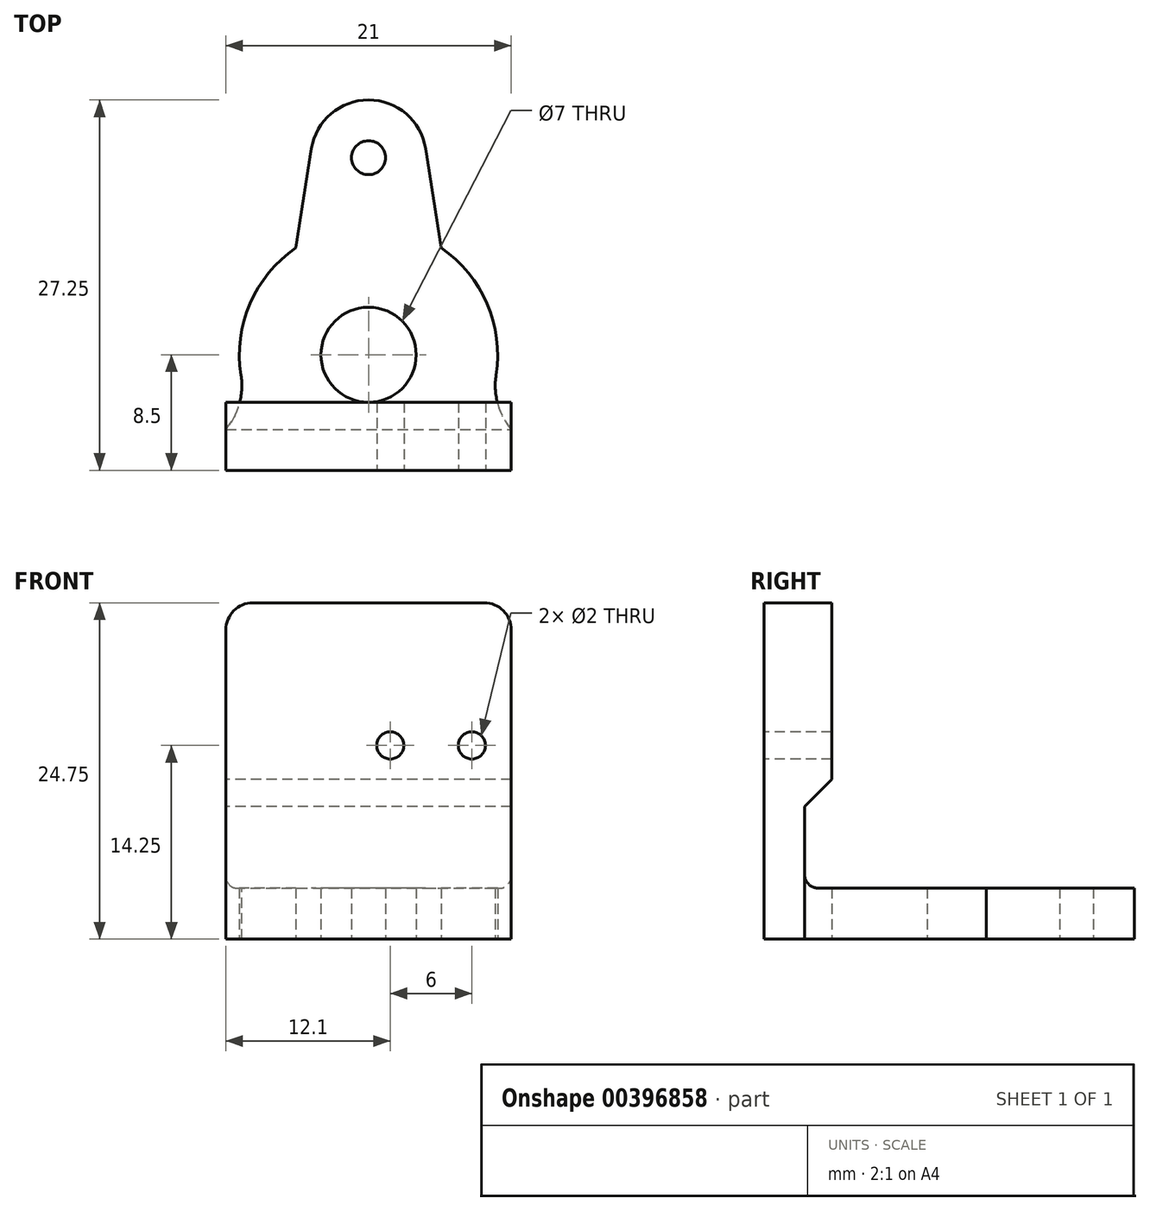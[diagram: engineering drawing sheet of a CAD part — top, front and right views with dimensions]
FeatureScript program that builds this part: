
annotation { "Feature Type Name" : "Feature", "Feature Type Description" : "" }
export const myFeature = defineFeature(function(context is Context, id is Id, definition is map)
    precondition{}
    {
        {
            var Q0;
            Q0=qCreatedBy(makeId("Top.planeOp"),FACE);
            var sketch = newSketch(context, id + "F0", { "sketchPlane" : qUnion([Q0])});
            skCircle(sketch, "E0", {"center": v(0, 0) * mm, "radius": 3.5 * mm});
            skCircle(sketch, "E1", {"center": v(0, 14.5) * mm, "radius": 1.25 * mm});
            skCircle(sketch, "E2", {"center": v(0, 0) * mm, "radius": 6.5 * mm});
            skLineSegment(sketch, "E3.bottom", {"start": v(6.5, 0) * mm, "end": v(-6.5, 0) * mm});
            skLineSegment(sketch, "E3.top", {"start": v(6.5, -8.5) * mm, "end": v(-6.5, -8.5) * mm});
            skLineSegment(sketch, "E3.left", {"start": v(6.5, -8.5) * mm, "end": v(6.5, 0) * mm});
            skLineSegment(sketch, "E3.right", {"start": v(-6.5, -8.5) * mm, "end": v(-6.5, 0) * mm});
            skCircle(sketch, "E4", {"center": v(0, 14.5) * mm, "radius": 4.25 * mm});
            skLineSegment(sketch, "E5", {"start": v(-6.42, 1) * mm, "end": v(-4.2, 15.16) * mm});
            skLineSegment(sketch, "E6", {"start": v(4.2, 15.16) * mm, "end": v(6.42, 1) * mm});
            skCircle(sketch, "E7", {"center": v(0, 0) * mm, "radius": 9.5 * mm});
            skSolve(sketch);
        }
        {
            var Q0;
            {var subQ0=sQuery(id+"F0.wireOp",EDGE,"E3.left");var subQ1=sQuery(id+"F0.wireOp",EDGE,"E3.top");var subQ2=makeQuery(id+"F0.imprint","INTERSECT",VERTEX,{"derivedFrom":[subQ1,subQ0]});Q0=makeQuery(id+"F0.imprint","IMPRINT",FACE,{"disambiguationData":[TD([[makeQuery(id+"F0.imprint","IMPRINT",EDGE,{"disambiguationData":[TD([[subQ2,-1.0]])],"derivedFrom":subQ1}),-1.0]])]});}
            var Q1;
            {var subQ0=sQuery(id+"F0.wireOp",EDGE,"E3.right");var subQ1=sQuery(id+"F0.wireOp",EDGE,"E3.top");var subQ2=makeQuery(id+"F0.imprint","INTERSECT",VERTEX,{"derivedFrom":[subQ1,subQ0]});Q1=makeQuery(id+"F0.imprint","IMPRINT",FACE,{"disambiguationData":[TD([[makeQuery(id+"F0.imprint","IMPRINT",EDGE,{"disambiguationData":[TD([[subQ2,1.0]])],"derivedFrom":subQ1}),-1.0]])]});}
            var Q2;
            Q2=makeQuery(id+"F0.imprint","IMPRINT",FACE,{"disambiguationData":[TD([[makeQuery(id+"F0.imprint","IMPRINT",EDGE,{"derivedFrom":sQuery(id+"F0.wireOp",EDGE,"E1")}),-1.0]])]});
            var Q3;
            {var subQ0=sQuery(id+"F0.wireOp",EDGE,"E5");var subQ1=sQuery(id+"F0.wireOp",EDGE,"E4");var subQ2=makeQuery(id+"F0.imprint","INTERSECT",VERTEX,{"derivedFrom":[subQ1,subQ0]});Q3=makeQuery(id+"F0.imprint","IMPRINT",FACE,{"disambiguationData":[TD([[makeQuery(id+"F0.imprint","IMPRINT",EDGE,{"disambiguationData":[TD([[subQ2,-1.0]])],"derivedFrom":subQ1}),-1.0]])]});}
            var Q4;
            {var subQ1=sQuery(id+"F0.wireOp",EDGE,"E2");var subQ3=sQuery(id+"F0.wireOp",EDGE,"E6");var subQ4=makeQuery(id+"F0.imprint","INTERSECT",VERTEX,{"derivedFrom":[subQ1,subQ3]});Q4=makeQuery(id+"F0.imprint","IMPRINT",FACE,{"disambiguationData":[TD([[makeQuery(id+"F0.imprint","IMPRINT",EDGE,{"disambiguationData":[TD([[subQ4,1.0]])],"derivedFrom":subQ3}),1.0]])]});}
            var Q5;
            {var subQ1=sQuery(id+"F0.wireOp",EDGE,"E2");var subQ3=sQuery(id+"F0.wireOp",EDGE,"E5");var subQ4=makeQuery(id+"F0.imprint","INTERSECT",VERTEX,{"derivedFrom":[subQ1,subQ3]});Q5=makeQuery(id+"F0.imprint","IMPRINT",FACE,{"disambiguationData":[TD([[makeQuery(id+"F0.imprint","IMPRINT",EDGE,{"disambiguationData":[TD([[subQ4,-1.0]])],"derivedFrom":subQ3}),1.0]])]});}
            var Q6;
            {var subQ0=sQuery(id+"F0.wireOp",EDGE,"E5");var subQ1=sQuery(id+"F0.wireOp",EDGE,"E2");var subQ2=makeQuery(id+"F0.imprint","INTERSECT",VERTEX,{"derivedFrom":[subQ1,subQ0]});Q6=makeQuery(id+"F0.imprint","IMPRINT",FACE,{"disambiguationData":[TD([[makeQuery(id+"F0.imprint","IMPRINT",EDGE,{"disambiguationData":[TD([[subQ2,1.0]])],"derivedFrom":subQ1}),-1.0]])]});}
            var Q7;
            {var subQ4=sQuery(id+"F0.wireOp",EDGE,"E7");var subQ6=sQuery(id+"F0.wireOp",EDGE,"E3.top");var subQ11=makeQuery(id+"F0.imprint","INTERSECT",VERTEX,{"disambiguationData":[OD(0.0)],"derivedFrom":[subQ6,subQ4]});Q7=makeQuery(id+"F0.imprint","IMPRINT",FACE,{"disambiguationData":[TD([[makeQuery(id+"F0.imprint","IMPRINT",EDGE,{"disambiguationData":[TD([[subQ11,-1.0]])],"derivedFrom":subQ6}),-1.0]])]});}
            var Q8;
            {var subQ0=sQuery(id+"F0.wireOp",EDGE,"E3.bottom");var subQ1=sQuery(id+"F0.wireOp",EDGE,"E0");var subQ2=makeQuery(id+"F0.imprint","INTERSECT",VERTEX,{"disambiguationData":[OD(0.0)],"derivedFrom":[subQ1,subQ0]});Q8=makeQuery(id+"F0.imprint","IMPRINT",FACE,{"disambiguationData":[TD([[makeQuery(id+"F0.imprint","IMPRINT",EDGE,{"disambiguationData":[TD([[subQ2,1.0]])],"derivedFrom":subQ1}),-1.0]])]});}
            var Q9;
            {var subQ3=sQuery(id+"F0.wireOp",EDGE,"E3.bottom");var subQ6=sQuery(id+"F0.wireOp",EDGE,"E0");var subQ7=makeQuery(id+"F0.imprint","INTERSECT",VERTEX,{"disambiguationData":[OD(0.0)],"derivedFrom":[subQ6,subQ3]});Q9=makeQuery(id+"F0.imprint","IMPRINT",FACE,{"disambiguationData":[TD([[makeQuery(id+"F0.imprint","IMPRINT",EDGE,{"disambiguationData":[TD([[subQ7,-1.0]])],"derivedFrom":subQ6}),-1.0]])]});}
            extrude(context, id + "F1", {"entities" : qUnion([Q0, Q1, Q2, Q3, Q4, Q5, Q6, Q7, Q8, Q9]), "depth" : 3.75 * mm});
        }
        {
            var Q0;
            Q0=makeQuery(id+"F1.opExtrude","SWEPT_FACE",FACE,{"disambiguationData":[OSD([sQuery(id+"F0.wireOp",EDGE,"E3.top")])]});
            cPlane(context, id + "F2", {"entities" : qUnion([Q0]), "cplaneType" : CPlaneType.OFFSET, "offset" : 0 * mm, "width" : 150 * mm, "height" : 150 * mm});
        }
        {
            var Q0;
            Q0=qCreatedBy(id+"F2.planeOp",FACE);
            var sketch = newSketch(context, id + "F3", { "sketchPlane" : qUnion([Q0])});
            skLineSegment(sketch, "E8.bottom", {"start": v(-10.5, 24.75) * mm, "end": v(10.5, 24.75) * mm});
            skLineSegment(sketch, "E8.top", {"start": v(-10.5, 3.75) * mm, "end": v(10.5, 3.75) * mm});
            skLineSegment(sketch, "E8.left", {"start": v(-10.5, 24.75) * mm, "end": v(-10.5, 3.75) * mm});
            skLineSegment(sketch, "E8.right", {"start": v(10.5, 24.75) * mm, "end": v(10.5, 3.75) * mm});
            skLineSegment(sketch, "E9.bottom", {"start": v(-6.5, 3.75) * mm, "end": v(6.5, 3.75) * mm});
            skLineSegment(sketch, "E9.top", {"start": v(-6.5, 0) * mm, "end": v(6.5, 0) * mm});
            skLineSegment(sketch, "E9.left", {"start": v(-6.5, 3.75) * mm, "end": v(-6.5, 0) * mm});
            skLineSegment(sketch, "E9.right", {"start": v(6.5, 3.75) * mm, "end": v(6.5, 0) * mm});
            skLineSegment(sketch, "E10", {"start": v(0, 24.75) * mm, "end": v(0, 0) * mm});
            skLineSegment(sketch, "E11.top", {"start": v(-10.5, 0) * mm, "end": v(10.5, 0) * mm});
            skLineSegment(sketch, "E11.left", {"start": v(-10.5, 3.75) * mm, "end": v(-10.5, 0) * mm});
            skLineSegment(sketch, "E11.right", {"start": v(10.5, 3.75) * mm, "end": v(10.5, 0) * mm});
            skSolve(sketch);
        }
        {
            var Q0;
            {var subQ0=sQuery(id+"F3.wireOp",EDGE,"E9.left");var subQ4=sQuery(id+"F3.wireOp",EDGE,"E8.left");var subQ12=sQuery(id+"F3.wireOp",EDGE,"E8.right");var subQ14=sQuery(id+"F3.wireOp",EDGE,"E9.right");var subQ23=makeQuery(id+"F3.imprint","IMPRINT",EDGE,{"derivedFrom":subQ14});var subQ24=makeQuery(id+"F3.imprint","IMPRINT",EDGE,{"derivedFrom":subQ0});Q0=qUnion([makeQuery(id+"F3.imprint","IMPRINT",FACE,{"disambiguationData":[TD([[subQ23,1.0]])]}),makeQuery(id+"F3.imprint","IMPRINT",FACE,{"disambiguationData":[TD([[subQ24,1.0]])]}),makeQuery(id+"F3.imprint","IMPRINT",FACE,{"disambiguationData":[TD([[subQ24,-1.0]])]}),makeQuery(id+"F3.imprint","IMPRINT",FACE,{"disambiguationData":[TD([[subQ23,-1.0]])]}),makeQuery(id+"F3.imprint","IMPRINT",FACE,{"disambiguationData":[TD([[makeQuery(id+"F3.imprint","IMPRINT",EDGE,{"derivedFrom":subQ12}),-1.0]])]}),makeQuery(id+"F3.imprint","IMPRINT",FACE,{"disambiguationData":[TD([[makeQuery(id+"F3.imprint","IMPRINT",EDGE,{"derivedFrom":subQ4}),1.0]])]})]);}
            extrude(context, id + "F4", {"entities" : qUnion([Q0]), "operationType" : NewBodyOperationType.ADD, "oppositeDirection" : true, "depth" : 3 * mm});
        }
        {
            var Q0;
            Q0=makeQuery(id+"F4.opExtrude","CAP_FACE",FACE,{"disambiguationData":[OSD([sQuery(id+"F3.wireOp",EDGE,"E8.bottom"),sQuery(id+"F3.wireOp",EDGE,"E8.left"),sQuery(id+"F3.wireOp",EDGE,"E8.right"),sQuery(id+"F3.wireOp",EDGE,"E9.top"),sQuery(id+"F3.wireOp",EDGE,"E11.top"),sQuery(id+"F3.wireOp",EDGE,"E11.left"),sQuery(id+"F3.wireOp",EDGE,"E11.right")])],"isStart":false});
            var sketch = newSketch(context, id + "F5", { "sketchPlane" : qUnion([Q0])});
            skLineSegment(sketch, "E12.bottom", {"start": v(-10.5, 24.75) * mm, "end": v(10.5, 24.75) * mm});
            skLineSegment(sketch, "E12.top", {"start": v(-10.5, 9.75) * mm, "end": v(10.5, 9.75) * mm});
            skLineSegment(sketch, "E12.left", {"start": v(-10.5, 24.75) * mm, "end": v(-10.5, 9.75) * mm});
            skLineSegment(sketch, "E12.right", {"start": v(10.5, 24.75) * mm, "end": v(10.5, 9.75) * mm});
            skSolve(sketch);
        }
        {
            var Q0;
            Q0=makeQuery(id+"F5.imprint","IMPRINT",FACE,{"disambiguationData":[TD([[makeQuery(id+"F5.imprint","IMPRINT",EDGE,{"derivedFrom":sQuery(id+"F5.wireOp",EDGE,"E12.bottom")}),1.0]])]});
            extrude(context, id + "F6", {"entities" : qUnion([Q0]), "operationType" : NewBodyOperationType.ADD, "depth" : 2 * mm});
        }
        {
            var Q0;
            Q0=makeQuery(id+"F6.boolean.opBoolean","MERGE",EDGE,{"derivedFrom":[makeQuery(id+"F4.opExtrude","SWEPT_EDGE",EDGE,{"disambiguationData":[OSD([sQuery(id+"F3.wireOp",EDGE,"E8.bottom"),sQuery(id+"F3.wireOp",EDGE,"E8.left")])]}),makeQuery(id+"F6.opExtrude","SWEPT_EDGE",EDGE,{"disambiguationData":[OSD([sQuery(id+"F5.wireOp",EDGE,"E12.bottom"),sQuery(id+"F5.wireOp",EDGE,"E12.right")])]})]});
            var Q1;
            Q1=makeQuery(id+"F6.boolean.opBoolean","MERGE",EDGE,{"derivedFrom":[makeQuery(id+"F4.opExtrude","SWEPT_EDGE",EDGE,{"disambiguationData":[OSD([sQuery(id+"F3.wireOp",EDGE,"E8.bottom"),sQuery(id+"F3.wireOp",EDGE,"E8.right")])]}),makeQuery(id+"F6.opExtrude","SWEPT_EDGE",EDGE,{"disambiguationData":[OSD([sQuery(id+"F5.wireOp",EDGE,"E12.bottom"),sQuery(id+"F5.wireOp",EDGE,"E12.left")])]})]});
            var Q2;
            Q2=makeQuery(id+"F6.boolean.opBoolean","MERGE",EDGE,{"derivedFrom":[makeQuery(id+"F4.opExtrude","SWEPT_EDGE",EDGE,{"disambiguationData":[OSD([sQuery(id+"F3.wireOp",EDGE,"E8.bottom"),sQuery(id+"F3.wireOp",EDGE,"E8.right")])]}),makeQuery(id+"F6.opExtrude","SWEPT_EDGE",EDGE,{"disambiguationData":[OSD([sQuery(id+"F5.wireOp",EDGE,"E12.bottom"),sQuery(id+"F5.wireOp",EDGE,"E12.left")])]})]});
            var Q3;
            Q3=makeQuery(id+"F6.boolean.opBoolean","MERGE",EDGE,{"derivedFrom":[makeQuery(id+"F4.opExtrude","SWEPT_EDGE",EDGE,{"disambiguationData":[OSD([sQuery(id+"F3.wireOp",EDGE,"E8.bottom"),sQuery(id+"F3.wireOp",EDGE,"E8.left")])]}),makeQuery(id+"F6.opExtrude","SWEPT_EDGE",EDGE,{"disambiguationData":[OSD([sQuery(id+"F5.wireOp",EDGE,"E12.bottom"),sQuery(id+"F5.wireOp",EDGE,"E12.right")])]})]});
            var Q4;
            Q4=makeQuery(id+"F4.boolean.opBoolean","MERGE",EDGE,{"derivedFrom":[makeQuery(id+"F1.opExtrude","CAP_EDGE",EDGE,{"disambiguationData":[OSD([sQuery(id+"F0.wireOp",EDGE,"E3.right")])],"isStart":false}),makeQuery(id+"F4.opExtrude","SWEPT_EDGE",EDGE,{"disambiguationData":[OSD([sQuery(id+"F3.wireOp",EDGE,"E8.top"),sQuery(id+"F3.wireOp",EDGE,"E9.bottom"),sQuery(id+"F3.wireOp",EDGE,"E9.left")])]})]});
            var Q5;
            Q5=makeQuery(id+"F4.boolean.opBoolean","MERGE",EDGE,{"derivedFrom":[makeQuery(id+"F1.opExtrude","CAP_EDGE",EDGE,{"disambiguationData":[OSD([sQuery(id+"F0.wireOp",EDGE,"E3.left")])],"isStart":false}),makeQuery(id+"F4.opExtrude","SWEPT_EDGE",EDGE,{"disambiguationData":[OSD([sQuery(id+"F3.wireOp",EDGE,"E8.top"),sQuery(id+"F3.wireOp",EDGE,"E9.bottom"),sQuery(id+"F3.wireOp",EDGE,"E9.right")])]})]});
            fillet(context, id + "F7", {"entities" : qUnion([Q0, Q1, Q2, Q3, Q4, Q5]), "radius" : 2 * mm, "tangentPropagation" : true, "allowEdgeOverflow" : false});
        }
        {
            var Q0;
            Q0=makeQuery(id+"F4.boolean.opBoolean","INTERSECT",EDGE,{"derivedFrom":[makeQuery(id+"F1.opExtrude","CAP_FACE",FACE,{"disambiguationData":[OSD([sQuery(id+"F0.wireOp",EDGE,"E0"),sQuery(id+"F0.wireOp",EDGE,"E1"),sQuery(id+"F0.wireOp",EDGE,"E3.top"),sQuery(id+"F0.wireOp",EDGE,"E3.left"),sQuery(id+"F0.wireOp",EDGE,"E3.right"),sQuery(id+"F0.wireOp",EDGE,"E4"),sQuery(id+"F0.wireOp",EDGE,"E5"),sQuery(id+"F0.wireOp",EDGE,"E6"),sQuery(id+"F0.wireOp",EDGE,"E7")])],"isStart":false}),makeQuery(id+"F4.opExtrude","CAP_FACE",FACE,{"disambiguationData":[OSD([sQuery(id+"F3.wireOp",EDGE,"E8.bottom"),sQuery(id+"F3.wireOp",EDGE,"E8.left"),sQuery(id+"F3.wireOp",EDGE,"E8.right"),sQuery(id+"F3.wireOp",EDGE,"E9.top"),sQuery(id+"F3.wireOp",EDGE,"E11.top"),sQuery(id+"F3.wireOp",EDGE,"E11.left"),sQuery(id+"F3.wireOp",EDGE,"E11.right")])],"isStart":false})]});
            fillet(context, id + "F8", {"entities" : qUnion([Q0]), "radius" : 1 * mm, "tangentPropagation" : true, "allowEdgeOverflow" : false});
        }
        {
            var Q0;
            Q0=makeQuery(id+"F6.opExtrude","CAP_EDGE",EDGE,{"disambiguationData":[OSD([sQuery(id+"F5.wireOp",EDGE,"E12.top")])],"isStart":false});
            chamfer(context, id + "F9", {"entities" : qUnion([Q0]), "width" : 2 * mm, "tangentPropagation" : true});
        }
        {
            var Q0;
            {var subQ0=sQuery(id+"F0.wireOp",EDGE,"E7");Q0=makeQuery(id+"F4.boolean.opBoolean","INTERSECT",EDGE,{"derivedFrom":[makeQuery(id+"F1.opExtrude","SWEPT_FACE",FACE,{"disambiguationData":[OSD([subQ0]),TDD([makeQuery(id+"F0.imprint","IMPRINT",EDGE,{"disambiguationData":[TD([[makeQuery(id+"F0.imprint","INTERSECT",VERTEX,{"derivedFrom":[sQuery(id+"F0.wireOp",EDGE,"E3.left"),subQ0]}),-1.0]])],"derivedFrom":subQ0})])]}),makeQuery(id+"F4.opExtrude","CAP_FACE",FACE,{"disambiguationData":[OSD([sQuery(id+"F3.wireOp",EDGE,"E8.bottom"),sQuery(id+"F3.wireOp",EDGE,"E8.left"),sQuery(id+"F3.wireOp",EDGE,"E8.right"),sQuery(id+"F3.wireOp",EDGE,"E9.top"),sQuery(id+"F3.wireOp",EDGE,"E11.top"),sQuery(id+"F3.wireOp",EDGE,"E11.left"),sQuery(id+"F3.wireOp",EDGE,"E11.right")])],"isStart":false})]});}
            var Q1;
            {var subQ0=sQuery(id+"F0.wireOp",EDGE,"E7");Q1=makeQuery(id+"F4.boolean.opBoolean","INTERSECT",EDGE,{"derivedFrom":[makeQuery(id+"F1.opExtrude","SWEPT_FACE",FACE,{"disambiguationData":[OSD([subQ0]),TDD([makeQuery(id+"F0.imprint","IMPRINT",EDGE,{"disambiguationData":[TD([[makeQuery(id+"F0.imprint","INTERSECT",VERTEX,{"derivedFrom":[sQuery(id+"F0.wireOp",EDGE,"E3.right"),subQ0]}),1.0]])],"derivedFrom":subQ0})])]}),makeQuery(id+"F4.opExtrude","CAP_FACE",FACE,{"disambiguationData":[OSD([sQuery(id+"F3.wireOp",EDGE,"E8.bottom"),sQuery(id+"F3.wireOp",EDGE,"E8.left"),sQuery(id+"F3.wireOp",EDGE,"E8.right"),sQuery(id+"F3.wireOp",EDGE,"E9.top"),sQuery(id+"F3.wireOp",EDGE,"E11.top"),sQuery(id+"F3.wireOp",EDGE,"E11.left"),sQuery(id+"F3.wireOp",EDGE,"E11.right")])],"isStart":false})]});}
            fillet(context, id + "F10", {"entities" : qUnion([Q0, Q1]), "radius" : 5 * mm, "tangentPropagation" : true, "allowEdgeOverflow" : false});
        }
        {
            var Q0;
            Q0=makeQuery(id+"F4.boolean.opBoolean","MERGE",FACE,{"derivedFrom":[makeQuery(id+"F1.opExtrude","SWEPT_FACE",FACE,{"disambiguationData":[OSD([sQuery(id+"F0.wireOp",EDGE,"E3.top")])]}),makeQuery(id+"F4.opExtrude","CAP_FACE",FACE,{"disambiguationData":[OSD([sQuery(id+"F3.wireOp",EDGE,"E8.bottom"),sQuery(id+"F3.wireOp",EDGE,"E8.left"),sQuery(id+"F3.wireOp",EDGE,"E8.right"),sQuery(id+"F3.wireOp",EDGE,"E9.top"),sQuery(id+"F3.wireOp",EDGE,"E11.top"),sQuery(id+"F3.wireOp",EDGE,"E11.left"),sQuery(id+"F3.wireOp",EDGE,"E11.right")])],"isStart":true})]});
            var sketch = newSketch(context, id + "F11", { "sketchPlane" : qUnion([Q0])});
            skCircle(sketch, "E13", {"center": v(1.6, 14.25) * mm, "radius": 1 * mm});
            skCircle(sketch, "E14", {"center": v(7.6, 14.25) * mm, "radius": 1 * mm});
            skLineSegment(sketch, "E15", {"start": v(-10.5, 14.25) * mm, "end": v(10.5, 14.25) * mm});
            skSolve(sketch);
        }
        {
            var Q0;
            {var subQ0=sQuery(id+"F11.wireOp",EDGE,"E15");var subQ1=sQuery(id+"F11.wireOp",EDGE,"E14");var subQ2=makeQuery(id+"F11.imprint","INTERSECT",VERTEX,{"disambiguationData":[OD(0.0)],"derivedFrom":[subQ1,subQ0]});Q0=makeQuery(id+"F11.imprint","IMPRINT",FACE,{"disambiguationData":[TD([[makeQuery(id+"F11.imprint","IMPRINT",EDGE,{"disambiguationData":[TD([[subQ2,-1.0]])],"derivedFrom":subQ1}),1.0]])]});}
            var Q1;
            {var subQ0=sQuery(id+"F11.wireOp",EDGE,"E15");var subQ1=sQuery(id+"F11.wireOp",EDGE,"E14");var subQ2=makeQuery(id+"F11.imprint","INTERSECT",VERTEX,{"disambiguationData":[OD(0.0)],"derivedFrom":[subQ1,subQ0]});Q1=makeQuery(id+"F11.imprint","IMPRINT",FACE,{"disambiguationData":[TD([[makeQuery(id+"F11.imprint","IMPRINT",EDGE,{"disambiguationData":[TD([[subQ2,1.0]])],"derivedFrom":subQ1}),1.0]])]});}
            var Q2;
            {var subQ0=sQuery(id+"F11.wireOp",EDGE,"E15");var subQ1=sQuery(id+"F11.wireOp",EDGE,"E13");var subQ2=makeQuery(id+"F11.imprint","INTERSECT",VERTEX,{"disambiguationData":[OD(0.0)],"derivedFrom":[subQ1,subQ0]});Q2=makeQuery(id+"F11.imprint","IMPRINT",FACE,{"disambiguationData":[TD([[makeQuery(id+"F11.imprint","IMPRINT",EDGE,{"disambiguationData":[TD([[subQ2,-1.0]])],"derivedFrom":subQ1}),1.0]])]});}
            var Q3;
            {var subQ0=sQuery(id+"F11.wireOp",EDGE,"E15");var subQ1=sQuery(id+"F11.wireOp",EDGE,"E13");var subQ2=makeQuery(id+"F11.imprint","INTERSECT",VERTEX,{"disambiguationData":[OD(0.0)],"derivedFrom":[subQ1,subQ0]});Q3=makeQuery(id+"F11.imprint","IMPRINT",FACE,{"disambiguationData":[TD([[makeQuery(id+"F11.imprint","IMPRINT",EDGE,{"disambiguationData":[TD([[subQ2,1.0]])],"derivedFrom":subQ1}),1.0]])]});}
            extrude(context, id + "F12", {"entities" : qUnion([Q0, Q1, Q2, Q3]), "operationType" : NewBodyOperationType.REMOVE, "endBound" : BoundingType.THROUGH_ALL, "oppositeDirection" : true, "depth" : 25 * mm});
        }
    });
